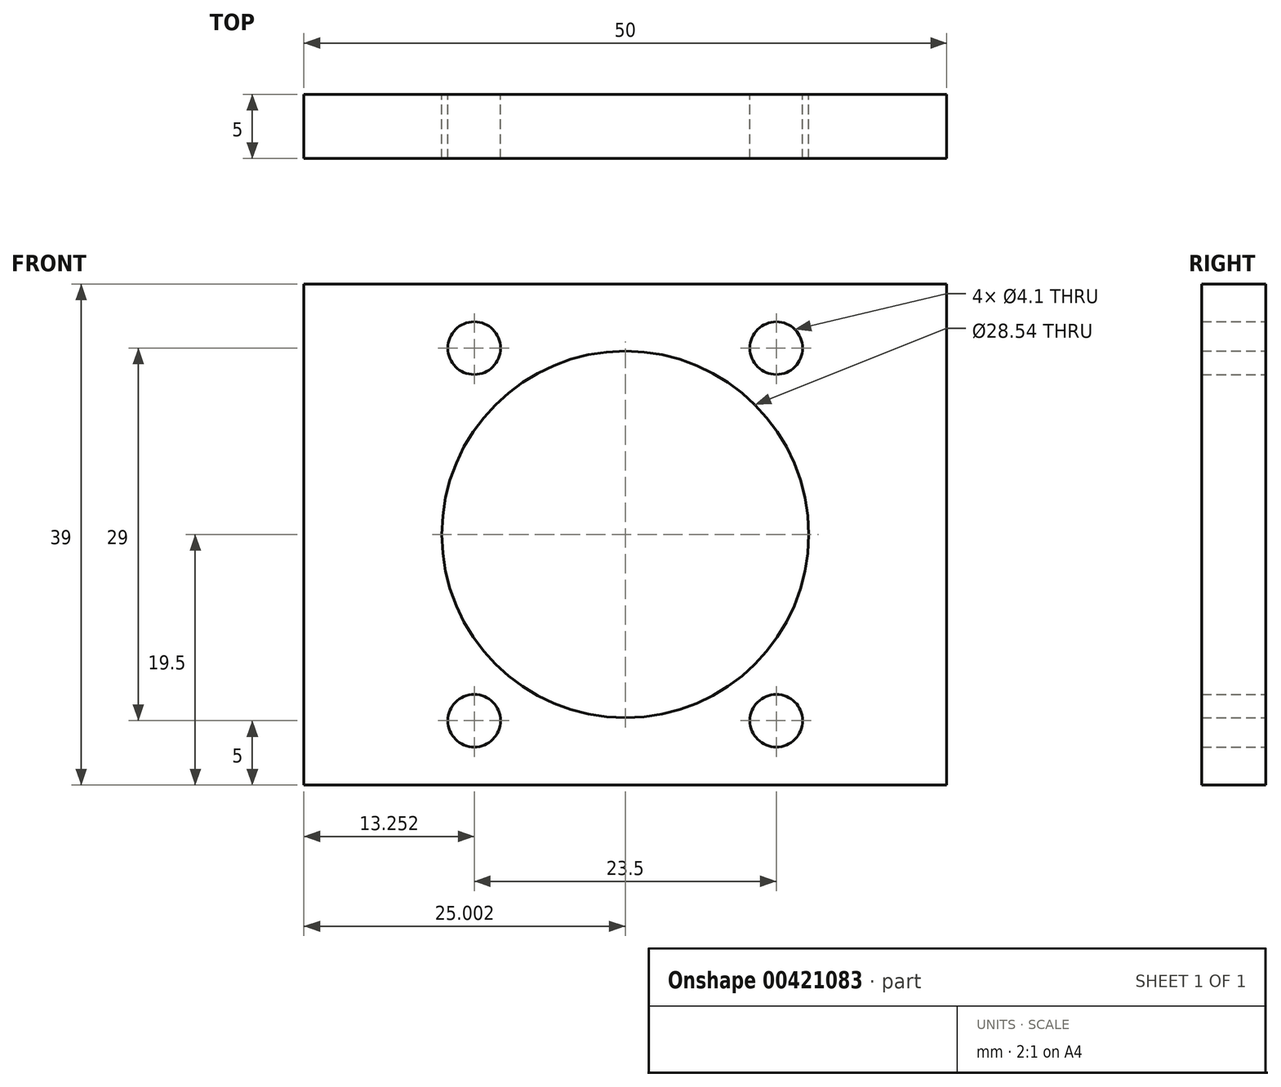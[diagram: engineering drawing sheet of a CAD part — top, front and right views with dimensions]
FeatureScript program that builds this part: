
annotation { "Feature Type Name" : "Feature", "Feature Type Description" : "" }
export const myFeature = defineFeature(function(context is Context, id is Id, definition is map)
    precondition{}
    {
        {
            var Q0;
            Q0=qCreatedBy(makeId("Front.planeOp"),FACE);
            var sketch = newSketch(context, id + "F0", { "sketchPlane" : qUnion([Q0])});
            skLineSegment(sketch, "E0.bottom", {"start": v(-48.78, 5) * mm, "end": v(-15.28, 5) * mm});
            skLineSegment(sketch, "E0.top", {"start": v(-48.78, -34) * mm, "end": v(-15.28, -34) * mm});
            skLineSegment(sketch, "E0.left", {"start": v(-48.78, 5) * mm, "end": v(-48.78, -34) * mm});
            skLineSegment(sketch, "E0.right", {"start": v(-15.28, 5) * mm, "end": v(-15.28, -34) * mm});
            skCircle(sketch, "E1", {"center": v(-32.03, -14.5) * mm, "radius": 14.27 * mm});
            skCircle(sketch, "E2", {"center": v(-43.78, 0) * mm, "radius": 2.05 * mm});
            skCircle(sketch, "E3", {"center": v(-20.28, 0) * mm, "radius": 2.05 * mm});
            skCircle(sketch, "E4", {"center": v(-20.28, -29) * mm, "radius": 2.05 * mm});
            skCircle(sketch, "E5", {"center": v(-43.78, -29) * mm, "radius": 2.05 * mm});
            skSolve(sketch);
        }
        {
            var Q0;
            Q0=makeQuery(id+"F0.imprint","IMPRINT",FACE,{"disambiguationData":[TD([[makeQuery(id+"F0.imprint","IMPRINT",EDGE,{"derivedFrom":sQuery(id+"F0.wireOp",EDGE,"E0.bottom")}),-1.0]])]});
            extrude(context, id + "F1", {"entities" : qUnion([Q0]), "depth" : 5 * mm});
        }
        {
            var Q0;
            Q0=makeQuery(id+"F1.opExtrude","CAP_FACE",FACE,{"disambiguationData":[OSD([sQuery(id+"F0.wireOp",EDGE,"E0.bottom"),sQuery(id+"F0.wireOp",EDGE,"E0.top"),sQuery(id+"F0.wireOp",EDGE,"E0.left"),sQuery(id+"F0.wireOp",EDGE,"E0.right"),sQuery(id+"F0.wireOp",EDGE,"E1"),sQuery(id+"F0.wireOp",EDGE,"E2"),sQuery(id+"F0.wireOp",EDGE,"E3"),sQuery(id+"F0.wireOp",EDGE,"E4"),sQuery(id+"F0.wireOp",EDGE,"E5")])],"isStart":false});
            var sketch = newSketch(context, id + "F2", { "sketchPlane" : qUnion([Q0])});
            skLineSegment(sketch, "E6.bottom", {"start": v(-48.78, 5) * mm, "end": v(-57.03, 5) * mm});
            skLineSegment(sketch, "E6.top", {"start": v(-48.78, -34) * mm, "end": v(-57.03, -34) * mm});
            skLineSegment(sketch, "E6.left", {"start": v(-48.78, 5) * mm, "end": v(-48.78, -34) * mm});
            skLineSegment(sketch, "E6.right", {"start": v(-57.03, 5) * mm, "end": v(-57.03, -34) * mm});
            skLineSegment(sketch, "E7.bottom", {"start": v(-15.28, 5) * mm, "end": v(-7.03, 5) * mm});
            skLineSegment(sketch, "E7.top", {"start": v(-15.28, -34) * mm, "end": v(-7.03, -34) * mm});
            skLineSegment(sketch, "E7.left", {"start": v(-15.28, 5) * mm, "end": v(-15.28, -34) * mm});
            skLineSegment(sketch, "E7.right", {"start": v(-7.03, 5) * mm, "end": v(-7.03, -34) * mm});
            skSolve(sketch);
        }
        {
            var Q0;
            Q0 = qSketchRegion(id + "F2", true);
            var Q1;
            Q1=makeQuery(id+"F1.opExtrude","CAP_VERTEX",VERTEX,{"disambiguationData":[OSD([sQuery(id+"F0.wireOp",EDGE,"E0.bottom"),sQuery(id+"F0.wireOp",EDGE,"E0.left")])],"isStart":true});
            extrude(context, id + "F3", {"entities" : qUnion([Q0]), "operationType" : NewBodyOperationType.ADD, "endBound" : BoundingType.UP_TO_VERTEX, "oppositeDirection" : true, "endBoundEntityVertex" : qUnion([Q1]), "depth" : 25 * mm});
        }
    });
